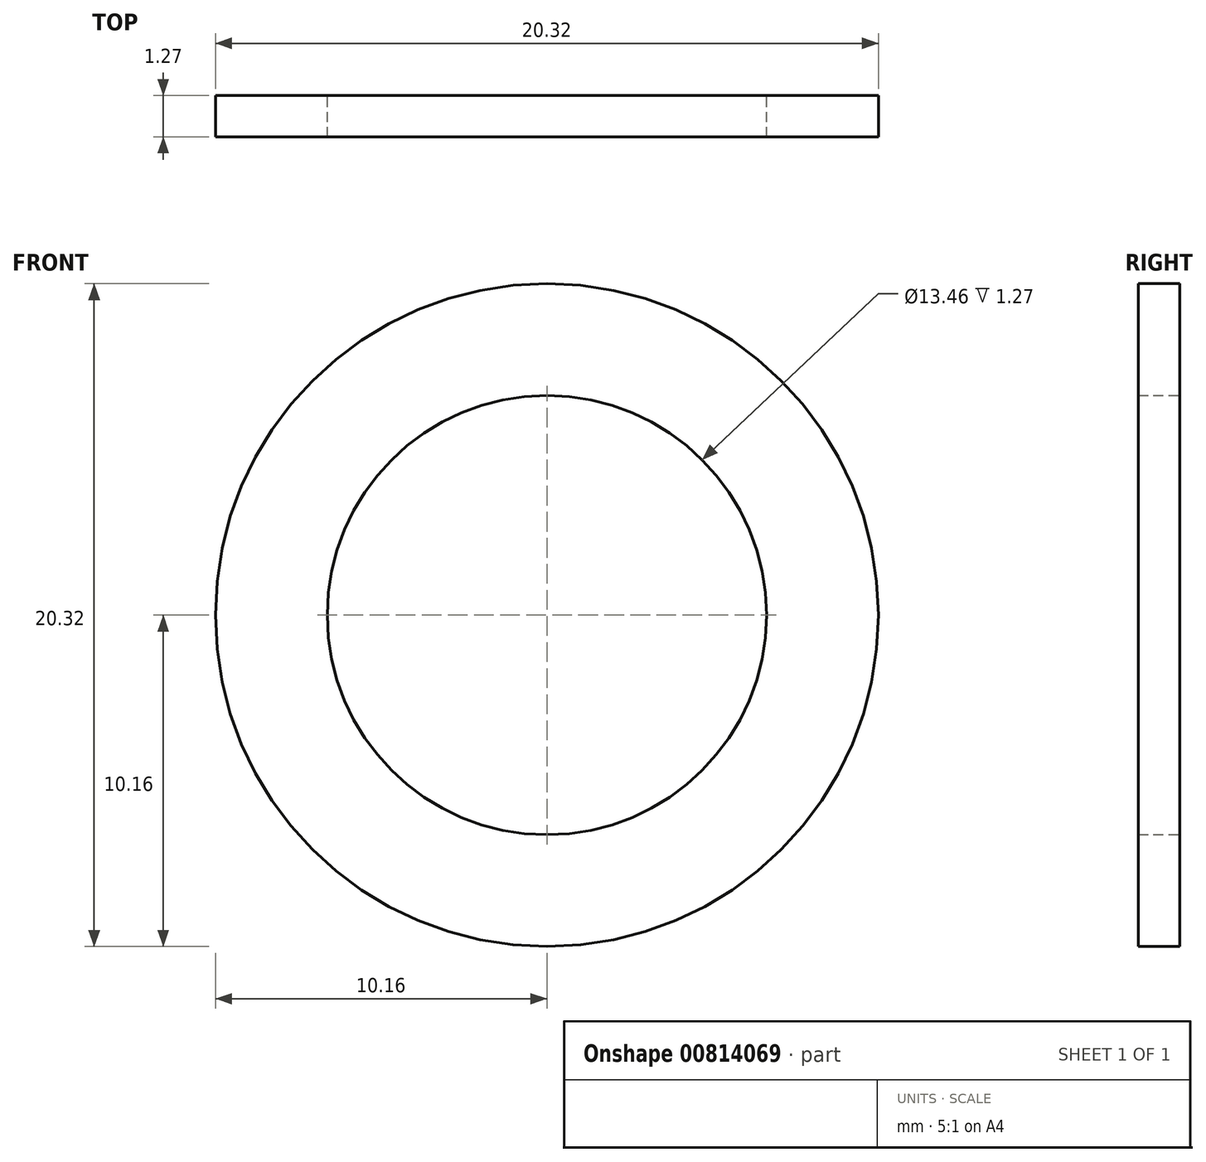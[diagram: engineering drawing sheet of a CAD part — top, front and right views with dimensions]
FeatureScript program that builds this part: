
annotation { "Feature Type Name" : "Feature", "Feature Type Description" : "" }
export const myFeature = defineFeature(function(context is Context, id is Id, definition is map)
    precondition{}
    {
        {
            var Q0;
            Q0=qCreatedBy(makeId("Front.planeOp"),FACE);
            var sketch = newSketch(context, id + "F0", { "sketchPlane" : qUnion([Q0])});
            skCircle(sketch, "E0", {"center": v(0, 0) * mm, "radius": 10.16 * mm});
            skCircle(sketch, "E1", {"center": v(0, 0) * mm, "radius": 6.73 * mm});
            skSolve(sketch);
        }
        {
            var Q0;
            Q0 = qSketchRegion(id + "F0", true);
            extrude(context, id + "F1", {"entities" : qUnion([Q0]), "depth" : 1.27 * mm, "offsetDistance" : 25.4 * mm});
        }
    });
